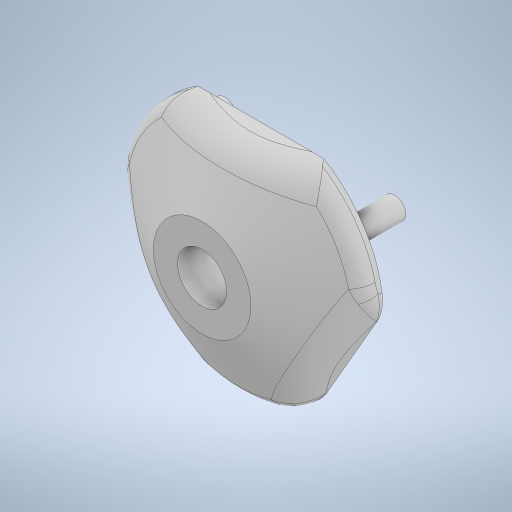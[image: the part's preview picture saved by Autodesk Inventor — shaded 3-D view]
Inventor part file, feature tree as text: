
AUTODESK INVENTOR PART (.ipt)
format: ipt  version: 2023 (Build 270158000, 158)  size: 404,480 bytes
history: native  units: in
note: dims shown in document units (in); Inventor stores cm internally (conversion verified against a paired STEP export)
features: extrude x1, pattern_circular x1, sketch x1, other x1
ambient origin geometry x8: Origin, YZ Plane, XZ Plane, XY Plane, X Axis, Y Axis, Z Axis, Center Point
bodies: Solid1 (feature_tree)
feature tree (4):
  extrude  "Extrusion1"  Depth=0.7874in
  pattern_circular  "Circular Pattern1"  [2 undecoded]
  sketch  "Sketch1"  dims[d0=0.1772in d1=0.7874in d2=0.3937in d3=0.0in d4=1.1811in d5=2.4737in]
  other  "Schnitt-Linear austragen5"
note: 2 required parameter values undecoded (feature->parameter linkage not recoverable at this tier; creation-order binding heuristic only, values carry confidence <= 0.55)
